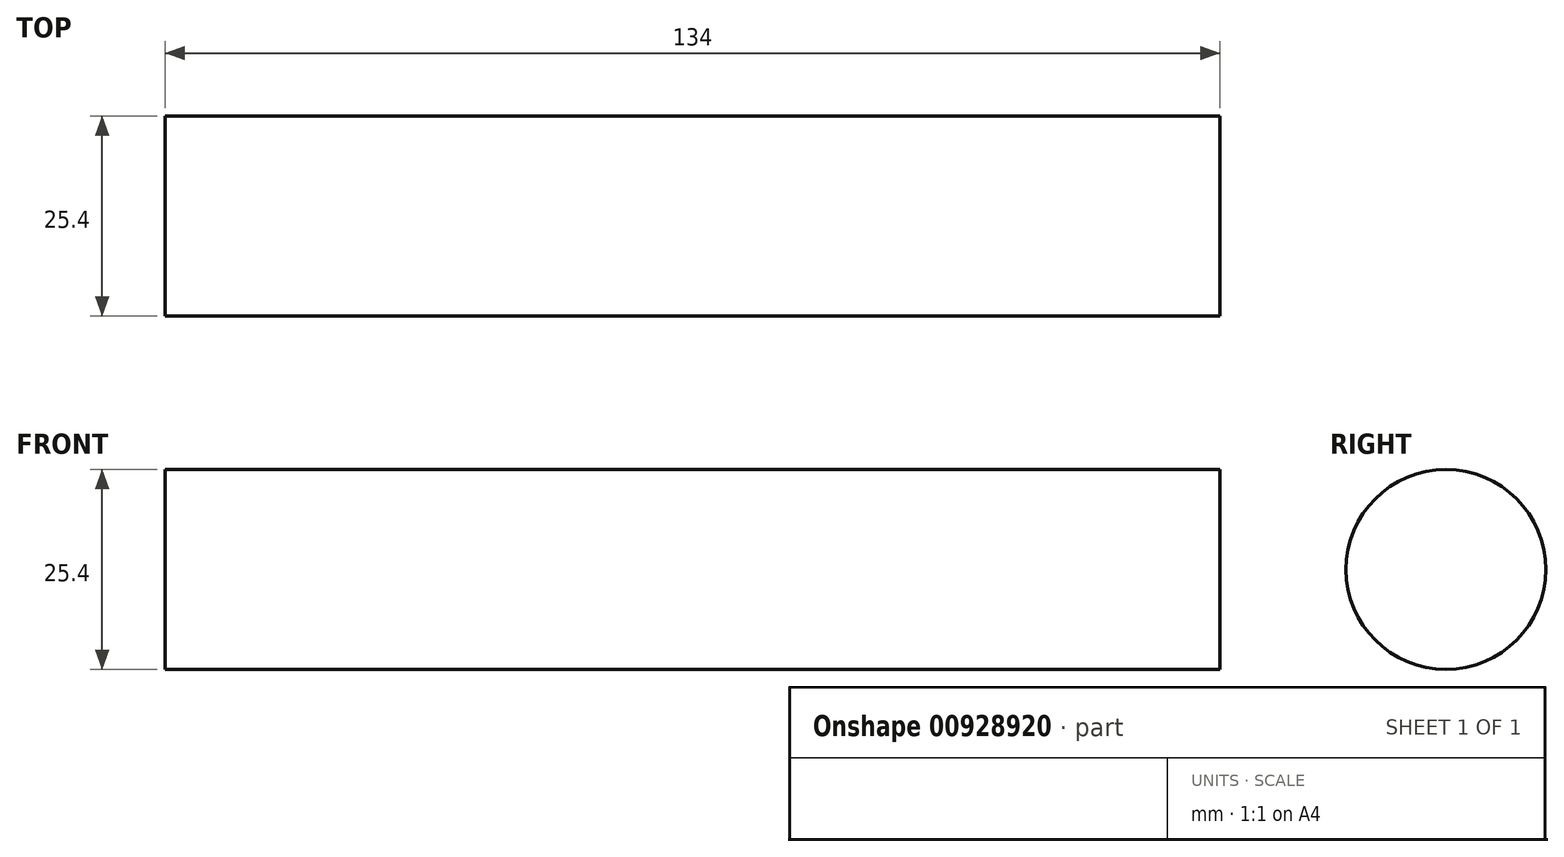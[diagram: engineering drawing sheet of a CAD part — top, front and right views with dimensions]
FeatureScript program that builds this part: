
annotation { "Feature Type Name" : "Feature", "Feature Type Description" : "" }
export const myFeature = defineFeature(function(context is Context, id is Id, definition is map)
    precondition{}
    {
        {
            var Q0;
            Q0=qCreatedBy(makeId("Front.planeOp"),FACE);
            var sketch = newSketch(context, id + "F0", { "sketchPlane" : qUnion([Q0])});
            skLineSegment(sketch, "E0", {"start": v(0, 0) * mm, "end": v(0, 12.7) * mm});
            skLineSegment(sketch, "E1", {"start": v(0, 12.7) * mm, "end": v(134, 12.7) * mm});
            skLineSegment(sketch, "E2", {"start": v(134, 12.7) * mm, "end": v(134, 0) * mm});
            skLineSegment(sketch, "E3", {"start": v(134, 0) * mm, "end": v(0, 0) * mm});
            skSolve(sketch);
        }
        {
            var Q0;
            Q0=makeQuery(id+"F0.imprint","IMPRINT",FACE,{"disambiguationData":[TD([[makeQuery(id+"F0.imprint","IMPRINT",EDGE,{"derivedFrom":sQuery(id+"F0.wireOp",EDGE,"E0")}),-1.0]])]});
            var Q1;
            Q1=sQuery(id+"F0.wireOp",EDGE,"E3");
            revolve(context, id + "F1", {"surfaceOperationType" : NewSurfaceOperationType.NEW, "entities" : qUnion([Q0]), "axis" : qUnion([Q1]), "revolveType" : RevolveType.FULL});
        }
    });
